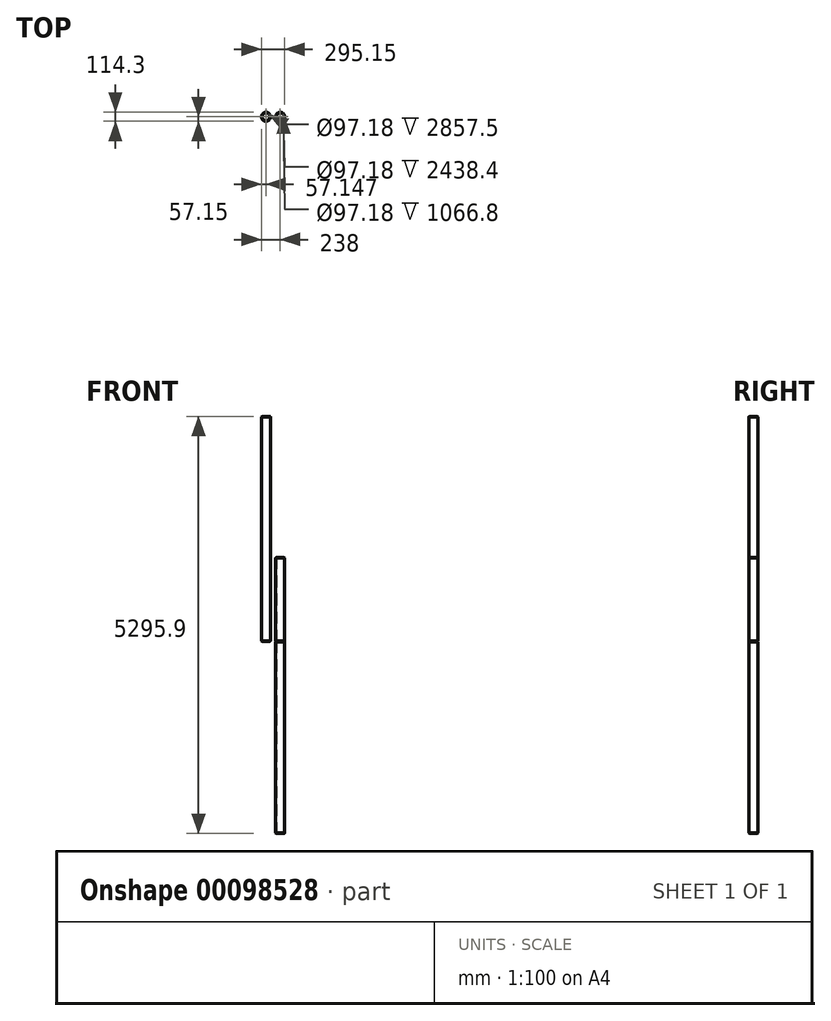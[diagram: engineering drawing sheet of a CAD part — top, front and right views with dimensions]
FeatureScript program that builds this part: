
annotation { "Feature Type Name" : "Feature", "Feature Type Description" : "" }
export const myFeature = defineFeature(function(context is Context, id is Id, definition is map)
    precondition{}
    {
        {
            var Q0;
            Q0=qCreatedBy(makeId("Front.planeOp"),FACE);
            var sketch = newSketch(context, id + "F0", { "sketchPlane" : qUnion([Q0])});
            skLineSegment(sketch, "E0", {"start": v(0, 0) * mm, "end": v(0, 1066.8) * mm, "construction": true});
            skLineSegment(sketch, "E1.left", {"start": v(57.15, 5.35) * mm, "end": v(57.15, 1061.45) * mm});
            skLineSegment(sketch, "E1.right", {"start": v(48.6, 0) * mm, "end": v(48.6, 1066.8) * mm});
            skLineSegment(sketch, "E2", {"start": v(50.18, 0) * mm, "end": v(57.15, 5.35) * mm});
            skLineSegment(sketch, "E3", {"start": v(50.18, 1066.8) * mm, "end": v(57.15, 1061.45) * mm});
            skLineSegment(sketch, "E4", {"start": v(48.6, 1066.8) * mm, "end": v(50.18, 1066.8) * mm});
            skLineSegment(sketch, "E5", {"start": v(48.6, 0) * mm, "end": v(50.18, 0) * mm});
            skSolve(sketch);
        }
        {
            var Q0;
            Q0=makeQuery(id+"F0.imprint","IMPRINT",FACE,{"disambiguationData":[TD([[makeQuery(id+"F0.imprint","IMPRINT",EDGE,{"derivedFrom":sQuery(id+"F0.wireOp",EDGE,"E1.left")}),1.0]])]});
            var Q1;
            Q1=sQuery(id+"F0.wireOp",EDGE,"E0");
            revolve(context, id + "F1", {"entities" : qUnion([Q0]), "axis" : qUnion([Q1]), "revolveType" : RevolveType.FULL});
        }
        {
            var Q0;
            Q0=qCreatedBy(makeId("Top.planeOp"),FACE);
            var sketch = newSketch(context, id + "F2", { "sketchPlane" : qUnion([Q0])});
            skCircle(sketch, "E6", {"center": v(0, 0) * mm, "radius": 57.15 * mm});
            skCircle(sketch, "E7", {"center": v(0, 0) * mm, "radius": 48.6 * mm});
            skCircle(sketch, "E8", {"center": v(0, 0) * mm, "radius": 50.18 * mm});
            skSolve(sketch);
        }
        {
            var Q0;
            Q0=qCreatedBy(makeId("Front.planeOp"),FACE);
            var sketch = newSketch(context, id + "F3", { "sketchPlane" : qUnion([Q0])});
            skLineSegment(sketch, "E9", {"start": v(0, 0) * mm, "end": v(0, -2438.4) * mm});
            skSolve(sketch);
        }
        {
            var Q0;
            Q0=makeQuery(id+"F2.imprint","IMPRINT",FACE,{"disambiguationData":[TD([[makeQuery(id+"F2.imprint","IMPRINT",EDGE,{"derivedFrom":sQuery(id+"F2.wireOp",EDGE,"E7")}),-1.0]])]});
            var Q1;
            Q1=makeQuery(id+"F2.imprint","IMPRINT",FACE,{"disambiguationData":[TD([[makeQuery(id+"F2.imprint","IMPRINT",EDGE,{"derivedFrom":sQuery(id+"F2.wireOp",EDGE,"E6")}),1.0]])]});
            var Q2;
            Q2=sQuery(id+"F3.wireOp",EDGE,"E9");
            sweep(context, id + "F4", {"profiles" : qUnion([Q0, Q1]), "path" : qUnion([Q2])});
        }
        {
            var Q0;
            Q0=makeQuery(id+"F4.opSweep","CAP_EDGE",EDGE,{"disambiguationData":[OSD([sQuery(id+"F2.wireOp",EDGE,"E6"),sQuery(id+"F3.wireOp",VERTEX,"E9.end")])],"isStart":false});
            chamfer(context, id + "F5", {"entities" : qUnion([Q0]), "chamferType" : ChamferType.TWO_OFFSETS, "width1" : 6.97 * mm, "oppositeDirection" : false, "width2" : 5.53 * mm, "tangentPropagation" : true});
        }
        {
            var Q0;
            Q0=makeQuery(id+"F4.opSweep","CAP_EDGE",EDGE,{"disambiguationData":[OSD([sQuery(id+"F2.wireOp",EDGE,"E6"),sQuery(id+"F3.wireOp",VERTEX,"E9.start")])],"isStart":true});
            chamfer(context, id + "F6", {"entities" : qUnion([Q0]), "chamferType" : ChamferType.TWO_OFFSETS, "width1" : 6.97 * mm, "oppositeDirection" : true, "width2" : 5.53 * mm, "tangentPropagation" : true});
        }
        {
            var Q0;
            Q0=qCreatedBy(makeId("Top.planeOp"),FACE);
            var sketch = newSketch(context, id + "F7", { "sketchPlane" : qUnion([Q0])});
            skCircle(sketch, "E10", {"center": v(-180.85, 0) * mm, "radius": 57.15 * mm});
            skCircle(sketch, "E11", {"center": v(-180.85, 0) * mm, "radius": 48.6 * mm});
            skSolve(sketch);
        }
        {
            var Q0;
            Q0=makeQuery(id+"F7.imprint","IMPRINT",FACE,{"disambiguationData":[TD([[makeQuery(id+"F7.imprint","IMPRINT",EDGE,{"derivedFrom":sQuery(id+"F7.wireOp",EDGE,"E10")}),1.0]])]});
            extrude(context, id + "F8", {"entities" : qUnion([Q0]), "depth" : 2857.5 * mm});
        }
        {
            var Q0;
            Q0=makeQuery(id+"F8.opExtrude","CAP_EDGE",EDGE,{"disambiguationData":[OSD([sQuery(id+"F7.wireOp",EDGE,"E10")])],"isStart":true});
            var Q1;
            Q1=makeQuery(id+"F8.opExtrude","CAP_EDGE",EDGE,{"disambiguationData":[OSD([sQuery(id+"F7.wireOp",EDGE,"E10")])],"isStart":false});
            chamfer(context, id + "F9", {"entities" : qUnion([Q0, Q1]), "chamferType" : ChamferType.TWO_OFFSETS, "width1" : 7 * mm, "oppositeDirection" : true, "width2" : 5.54 * mm, "tangentPropagation" : true});
        }
    });
